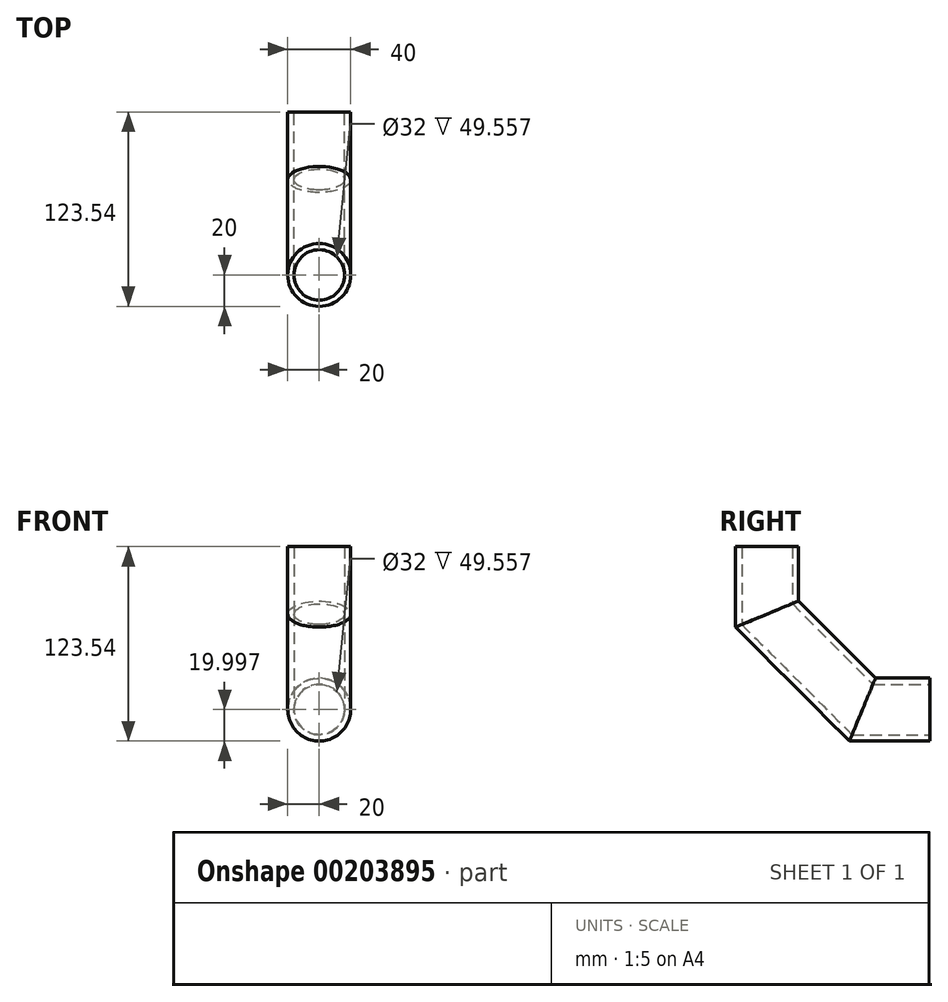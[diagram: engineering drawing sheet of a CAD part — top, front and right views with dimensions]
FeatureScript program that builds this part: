
annotation { "Feature Type Name" : "Feature", "Feature Type Description" : "" }
export const myFeature = defineFeature(function(context is Context, id is Id, definition is map)
    precondition{}
    {
        {
            var Q0;
            Q0=qCreatedBy(makeId("Top.planeOp"),FACE);
            var sketch = newSketch(context, id + "F0", { "sketchPlane" : qUnion([Q0])});
            skCircle(sketch, "E0", {"center": v(0, 0) * mm, "radius": 16 * mm});
            skCircle(sketch, "E1", {"center": v(0, 0) * mm, "radius": 20 * mm});
            skSolve(sketch);
        }
        {
            var Q0;
            Q0=qCreatedBy(makeId("Right.planeOp"),FACE);
            var sketch = newSketch(context, id + "F1", { "sketchPlane" : qUnion([Q0])});
            skLineSegment(sketch, "E2", {"start": v(0, 0) * mm, "end": v(0, -42.93) * mm});
            skLineSegment(sketch, "E3", {"start": v(0, -42.93) * mm, "end": v(60.62, -103.54) * mm});
            skLineSegment(sketch, "E4", {"start": v(60.62, -103.54) * mm, "end": v(103.54, -103.54) * mm});
            skSolve(sketch);
        }
        {
            var Q0;
            Q0=makeQuery(id+"F0.imprint","IMPRINT",FACE,{"disambiguationData":[TD([[makeQuery(id+"F0.imprint","IMPRINT",EDGE,{"derivedFrom":sQuery(id+"F0.wireOp",EDGE,"E0")}),-1.0]])]});
            var Q1;
            Q1=sQuery(id+"F1.wireOp",EDGE,"E2");
            var Q2;
            Q2=sQuery(id+"F1.wireOp",EDGE,"E3");
            var Q3;
            Q3=sQuery(id+"F1.wireOp",EDGE,"E4");
            sweep(context, id + "F2", {"profiles" : qUnion([Q0]), "path" : qUnion([Q1, Q2, Q3])});
        }
    });
